# Revit family: 400_57_BHT_Skyline_3000_60_CONC-PAR_(alu-pp_zwart-terra)_60-100
name_source: partatom
category: Air Terminals
revit_build: Autodesk Revit 2013 (Build: 20121003_2115(x64)
units: mm (PartAtom-declared; Revit-internal decimal feet)

## types (6) — shared parameters
Assembly Code = 3A(57)
IfcExportAs = IfcAirTerminal
IfcExportType = EYEBALL
Manufacturer = Burgerhout
Model = LOD400
URL = http://catalogus.burgerhout.nl
buitendiameter = 100 mm  [stored 0.328084 ft]
diameter = 60 mm  [stored 0.19685 ft]
product_serie = Skyline 3000

## per-type parameters (varying)
| type | Description | EAN_code | GTIN_Code | IfcDescription | artikelnummer | broekstuk | buitenzijde_materiaal | gewicht_kg | lengte | materiaal | max_medium_temperatuur | s_c | type_index | werkende_lengte |
| HR AL CONC 60/100 zwart | Skyline 3000 dakdoorvoer HR AL CONC 60/100 zwart | 08712799029621 | 08712799029621 | Skyline 3000 dakdoorvoer HR AL CONC 60/100 zwart | 400452740 | No | BHT_aluminium_zwart | 3.19 kg | 1290 mm  [stored 4.23228 ft] | BHT_aluminium | 120 °C | 0 mm  [stored 0 ft] | 0 | 1270 mm |
| HR PP CONC 60/100 zwart | Skyline 3000 dakdoorvoer HR PP CONC 60/100 zwart | 08712798029638 | 08712798029638 | Skyline 3000 dakdoorvoer HR PP CONC 60/100 zwart | 400452742 | No | BHT_aluminium_zwart | 2.66 kg | 1290 mm  [stored 4.23228 ft] | BHT_PP | 120 °C | 0 mm  [stored 0 ft] | 1 | 1270 mm |
| HR ALU CONC 60/100 terra | Skyline 3000 dakdoorvoer HR AL CONC 60/100 terra | 08712798029645 | 08712798029645 | Skyline 3000 dakdoorvoer HR AL CONC 60/100 terra | 400452743 | No | BHT_aluminium_terra | 3.48 kg | 1290 mm  [stored 4.23228 ft] | BHT_aluminium | 120 °C | 0 mm  [stored 0 ft] | 2 | 1270 mm |
| HR PP CONC 60/100 terra | Skyline 3000 dakdoorvoer HR PP CONC 60/100 terra | 08712798029652 | 08712798029652 | Skyline 3000 dakdoorvoer HR PP CONC 60/100 terra | 400452745 | No | BHT_aluminium_terra | 2.64 kg | 1290 mm  [stored 4.23228 ft] | BHT_PP | 120 °C | 0 mm  [stored 0 ft] | 3 | 1270 mm |
| ALU PAR 60/100 zwart | Skyline 3000 dakdoorvoer AL PAR 60/100 zwart | 08712798508812 | 08712798508812 | Skyline 3000 dakdoorvoer AL PAR 60/100 zwart | 400452739 | Yes | BHT_aluminium_zwart | 3.19 kg | 1400 mm | BHT_aluminium | 250 °C | 120 mm  [stored 0.393701 ft] | 4 | 1380 mm |
| PP PAR 60/100 zwart | Skyline 3000 dakdoorvoer PP PAR 60/100 zwart | 08712798508829 | 08712798508829 | Skyline 3000 dakdoorvoer PP PAR 60/100 zwart | 400452741 | Yes | BHT_aluminium_zwart | 2.66 kg | 1400 mm | BHT_PP | 250 °C | 120 mm  [stored 0.393701 ft] | 5 | 1380 mm |

note: [stored X ft] marks values corroborated as IEEE doubles in the binary element streams (Revit-internal decimal feet)

## geometry (parser evidence)
native form markers: Blend x16, Sweep x4
no freeform markers — native parametric forms only
